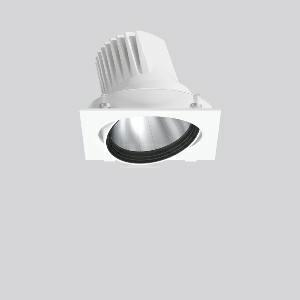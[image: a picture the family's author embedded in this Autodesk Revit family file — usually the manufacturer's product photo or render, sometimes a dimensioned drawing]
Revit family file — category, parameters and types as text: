
# Revit family: magcardo_maxi_722203_002_1c35
name_source: partatom
category: Lighting Fixtures
units: mm (PartAtom-declared; Revit-internal decimal feet)

## family parameters
Cut with Voids When Loaded = No
Host = Face
Light Source = No
Part Type = Normal
Room Calculation Point = No
Round Connector Dimension = Use Diameter
Shared = No

## types (1)
- MAGCARDO maxi (1 x LED Modul 932 fresh meat, 2050 lm, 3200)
    Apparent Load = 33 VA
    Approval mark = CE
    CIE Flux Codes = 96 100 100 100 100
    Color Rendering = 90
    Color Temperature = 3200
    Default Elevation = 1800 mm
    Description = Series: MAGCARDO maxi
Projector unit for tool-free mounting in separate recessed frame. Luminaire top: die-cast aluminium, powder-coated. Rotation range 356° and swivel range ± 35°. Inner cover prevents view into the false ceiling. Black plastic ring and recessed LED to prevent glare from the side. Optical assembly with reflector made of MIRO-Silver with 98% total light reflection for outstanding efficiency - can be changed without tools. Special LED for illumination of meat included. Magnetic click locking mechanism for quick and convenient installation without tools: insert the recessed frame (1, 2 or 3-lamp) with clamp fastener (no tools required), push the luminaire head with the base plate into the recessed frame and fix magnetically. Including separate LED converter with connecting cable 600 mm.High quality converter without flickering and stroboscopic effect. Through-wiring box (5 pole) available as accessory. The following accessories can be mounted without use of tools: interchangeable lenses, honeycomb louvre, clear and frosted diffusers, white interchangeable plastic ring.Modular design: recessed mounting frame must be ordered separately! 
Colour: traffic white, matt (RAL 9016)
Length: 172 mm
Width: 167 mm
Height: 137 mm
Recess height: 155 mm
Lamp: LED
Socket: without socket
Colour temperature: fresh meat
System power: 33 W
Rated luminous flux: 2050 lm
Luminous efficiency: 62 lm/W
Control gear: Regulated power supply
Protection class: II
Type of protection: IP 20
    Height = 0 mm  [stored 0 ft]
    Lamp = 1 x LED Modul 932 fresh meat
    Lamp Light Flux = 2050 lm
    Lamp count = 1
    Length = 172 mm
    Lifetime = 50000 h
    Luminous efficacy = 62 lm/W
    Manufacturer = RZB
    ModVariant = No
    Model = 722203.002
    Mounting Place = Ceiling, Wall
    Mounting Type = Recessed
    Number of Poles = 1
    OnlyDefault = Yes
    Power Factor = 1
    Product Name = MAGCARDO maxi
    Product group = Recessed projectors
    ProductGroupID = 401
    Protection Class = Protection class II
    Protection Degree = IP 20
    RLX_Detail_Level = 1
    RLX_Emergency_Light_Flux = 0 lm
    RLX_Emergency_Type = 0
    RLX_Emergency_Type_DB = No
    RlxData = <blob elided: 40777 chars, md5=c7ed415e>
    Socket = socket
    Standby Power = 0 W
    System Light Flux = 2050 lm
    System Power = 33 W
    Type Comments = Product without accessories
    Type Image = 722045.002.jpg
    URL = http://relux.com
    VarID = ---
    Voltage = 230 V
    Voltage Range = 220-240 V
    Weight = 0.00 kg
    Width = 167 mm

note: [stored X ft] marks values corroborated as IEEE doubles in the binary element streams (Revit-internal decimal feet)

## geometry (parser evidence)
native form markers: Blend x4, Sweep x12
no freeform markers — native parametric forms only
